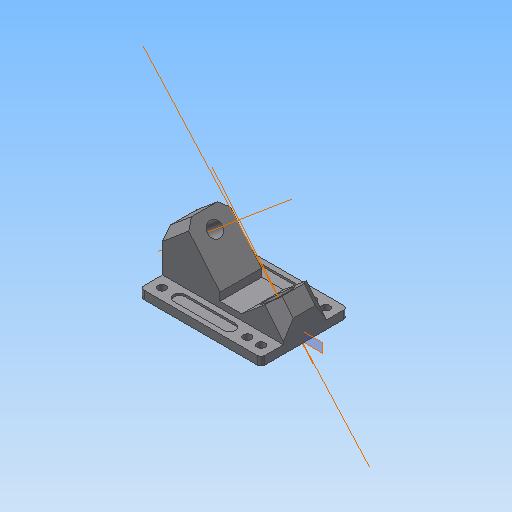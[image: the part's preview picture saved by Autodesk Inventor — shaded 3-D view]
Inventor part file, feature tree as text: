
AUTODESK INVENTOR PART (.ipt)
format: ipt  version: 2017 (Build 210142000, 142)  size: 346,112 bytes
history: native  units: in
note: dims shown in document units (in); Inventor stores cm internally (conversion verified against a paired STEP export)
features: sketch x15, extrude x13, projected_geometry x9, plane x3, chamfer x3, other x3, mirror x1, draft x1, fillet x1
ambient origin geometry x8: Origin, YZ Plane, XZ Plane, XY Plane, X Axis, Y Axis, Z Axis, Center Point
bodies: Solid1 (feature_tree)
feature tree (49):
  extrude  "Extrusion1"  Depth=2.2in
  plane  "Work Plane1"
  extrude  "Extrusion2"  Depth=0.21in TaperAngle=0.0deg
  extrude  "Extrusion3"  Depth=0.205in
  mirror  "Mirror1"
  extrude  "Extrusion4"  Depth=0.278in
  extrude  "Extrusion5"  Depth=0.278in
  extrude  "Extrusion6"  Depth=0.278in
  chamfer  "Chamfer1"  Distance=0.21in
  extrude  "Extrusion7"  Depth=0.3in
  chamfer  "Chamfer2"  Distance=0.05in
  other  "Work Axis1"
  extrude  "Extrusion8"  Depth=0.57in
  extrude  "Extrusion9"  Depth=1.06in
  chamfer  "Chamfer3"  Distance=0.65in
  extrude  "Extrusion10"  Depth=0.3436in
  draft  "FaceDraft5"
  extrude  "Extrusion11"  Depth=0.25in TaperAngle=45.0deg
  sketch  "Sketch14"  dims[d24=0.15in d25=0.0in d26=1.06in d27=0.65in d28=0.0in]
  sketch  "Sketch15"  dims[d34=0.3436in d35=0.3436in]
  extrude  "Extrusion13"  Depth=0.5in
  fillet  "Fillet2"  Radius=0.5in
  other  "Work Axis2"
  extrude  "Extrusion14"  Depth=0.25in TaperAngle=45.0deg
  plane  "Work Plane4"
  sketch  "Sketch18"  dims[d41=0.7in d42=0.5in d43=0.5in d44=0.0in d46=0.25in d47=0.125in d48=45.0deg d49=1.46in d50=1.3in d51=0.0in d52=0.2in d53=0.3436in d54=0.3436in d55=1.3in d56=0.0in d57=0.2in d58=0.125in d59=45.0deg d63=0.66in d64=0.125in d65=0.4in d66=0.0in d67=0.3436in d68=0.37in d69=0.4in d70=0.0in d71=1.1in d72=0.76in d73=0.0in d74=0.11in d75=0.8in d76=0.8933in d77=90.0deg d78=0.4in d79=0.4in d82=0.76in d83=0.0in d84=0.135in d85=1.08in d86=0.75in d87=0.05in d88=0.05in d89=0.5in d90=0.03in d91=0.0in d92=0.0137in]
  other  "Work Axis3"
  sketch  "Sketch1"  dims[d0=3.074in d1=2.2in]
  sketch  "Sketch2"  dims[d2=0.1in d3=0.21in d4=0.0in]
  sketch  "Sketch3"  dims[d5=0.205in d6=0.205in]
  plane  "Work Plane2"
  sketch  "Sketch4"  dims[d7=0.205in d8=0.278in]
  projected_geometry  "Projected Loop1"
  sketch  "Sketch5"  dims[d9=0.278in d10=0.278in]
  projected_geometry  "Projected Loop2"
  sketch  "Sketch8"  dims[d11=0.278in d12=0.278in]
  projected_geometry  "Projected Loop4"
  sketch  "Sketch9"  dims[d13=0.35in d14=0.21in d15=0.0in]
  sketch  "Sketch10"  dims[d16=0.3in d17=0.45in]
  projected_geometry  "Projected Loop5"
  sketch  "Sketch11"  dims[d18=0.45in]
  projected_geometry  "Projected Loop6"
  sketch  "Sketch12"  dims[d19=0.0in d20=0.05in d21=0.0in]
  projected_geometry  "Projected Loop7"
  sketch  "Sketch13"  dims[d22=0.57in d23=0.57in]
  projected_geometry  "Projected Loop8"
  projected_geometry  "Projected Loop9"
  projected_geometry  "Projected Loop10"
  sketch  "Sketch17"  dims[d36=0.75in d37=0.0in d38=0.25in d39=0.125in d40=45.0deg]
